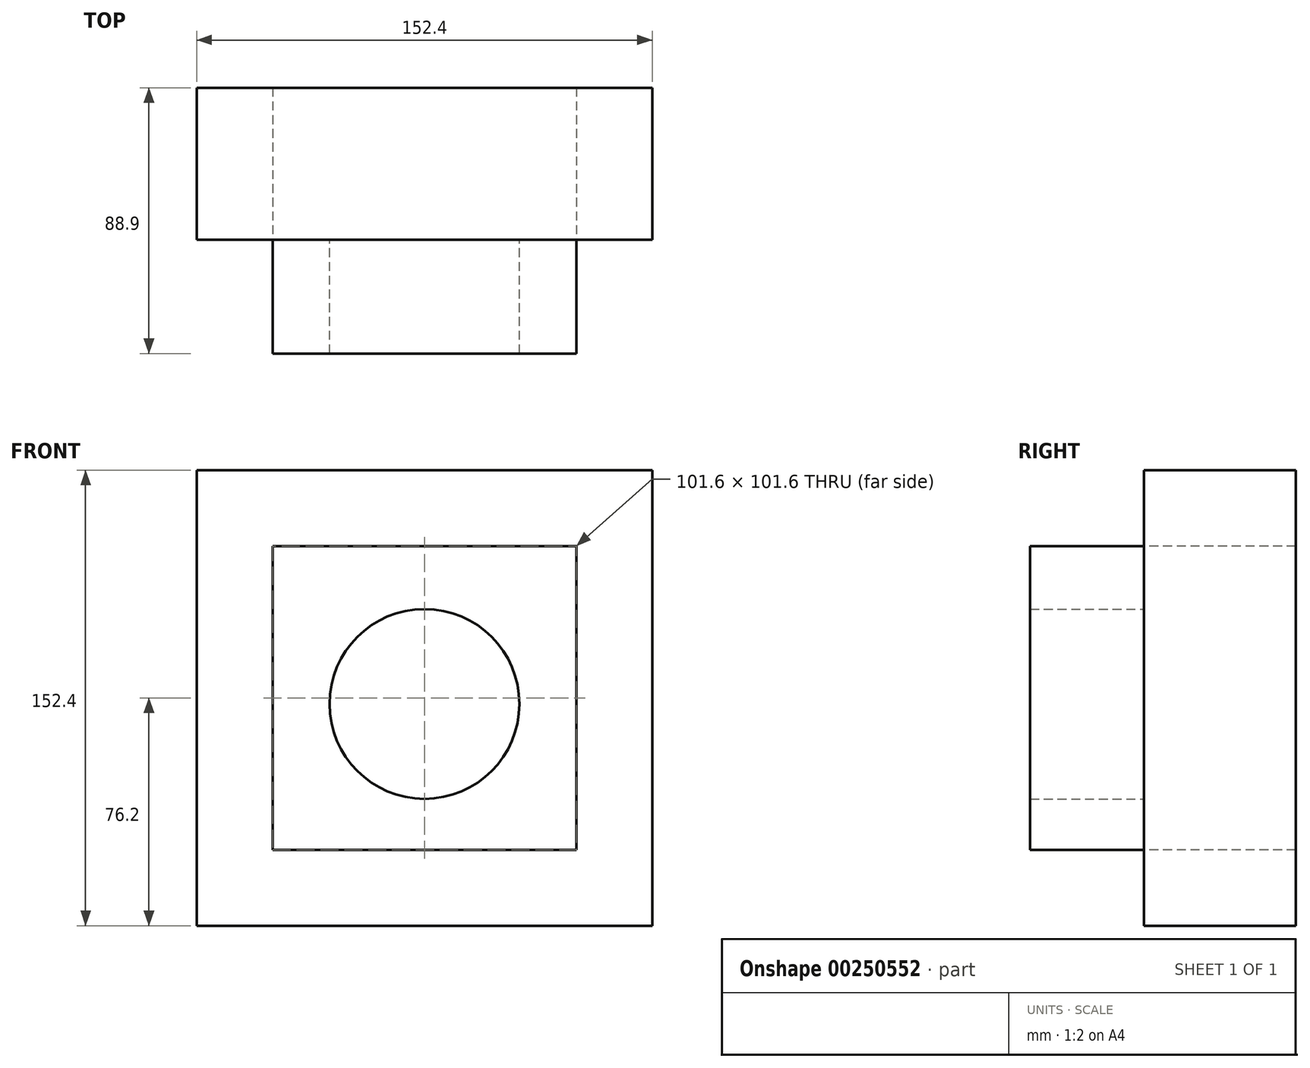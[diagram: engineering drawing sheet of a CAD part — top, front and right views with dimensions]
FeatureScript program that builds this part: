
annotation { "Feature Type Name" : "Feature", "Feature Type Description" : "" }
export const myFeature = defineFeature(function(context is Context, id is Id, definition is map)
    precondition{}
    {
        {
            var Q0;
            Q0=qCreatedBy(makeId("Front.planeOp"),FACE);
            var sketch = newSketch(context, id + "F0", { "sketchPlane" : qUnion([Q0])});
            skCircle(sketch, "E0", {"center": v(0, -2.03) * mm, "radius": 31.75 * mm});
            skLineSegment(sketch, "E1.bottom", {"start": v(50.8, 50.8) * mm, "end": v(-50.8, 50.8) * mm});
            skLineSegment(sketch, "E1.top", {"start": v(50.8, -50.8) * mm, "end": v(-50.8, -50.8) * mm});
            skLineSegment(sketch, "E1.left", {"start": v(50.8, 50.8) * mm, "end": v(50.8, -50.8) * mm});
            skLineSegment(sketch, "E1.right", {"start": v(-50.8, 50.8) * mm, "end": v(-50.8, -50.8) * mm});
            skPoint(sketch, "E1.middle", {"position": v(0, 0) * mm});
            skLineSegment(sketch, "E2.bottom", {"start": v(76.2, 76.2) * mm, "end": v(-76.2, 76.2) * mm});
            skLineSegment(sketch, "E2.top", {"start": v(76.2, -76.2) * mm, "end": v(-76.2, -76.2) * mm});
            skLineSegment(sketch, "E2.left", {"start": v(76.2, 76.2) * mm, "end": v(76.2, -76.2) * mm});
            skLineSegment(sketch, "E2.right", {"start": v(-76.2, 76.2) * mm, "end": v(-76.2, -76.2) * mm});
            skSolve(sketch);
        }
        {
            var Q0;
            Q0=makeQuery(id+"F0.imprint","IMPRINT",FACE,{"disambiguationData":[TD([[makeQuery(id+"F0.imprint","IMPRINT",EDGE,{"derivedFrom":sQuery(id+"F0.wireOp",EDGE,"E0")}),-1.0]])]});
            extrude(context, id + "F1", {"entities" : qUnion([Q0]), "depth" : 38.1 * mm});
        }
        {
            var Q0;
            Q0=makeQuery(id+"F0.imprint","IMPRINT",FACE,{"disambiguationData":[TD([[makeQuery(id+"F0.imprint","IMPRINT",EDGE,{"derivedFrom":sQuery(id+"F0.wireOp",EDGE,"E1.bottom")}),-1.0]])]});
            extrude(context, id + "F2", {"entities" : qUnion([Q0]), "oppositeDirection" : true, "depth" : 50.8 * mm});
        }
    });
